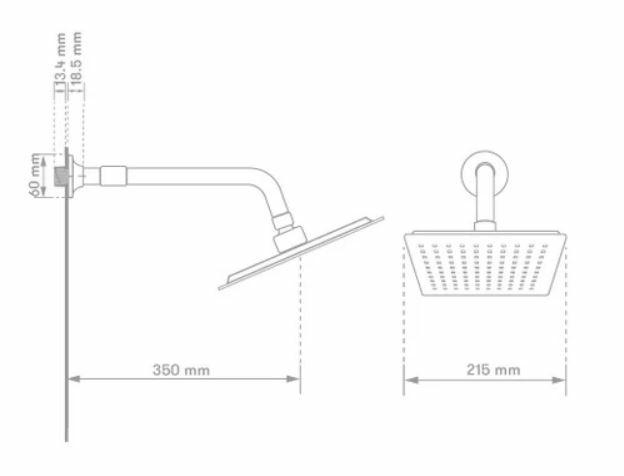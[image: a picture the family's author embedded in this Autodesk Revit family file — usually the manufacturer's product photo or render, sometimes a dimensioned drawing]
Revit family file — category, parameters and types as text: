
# Revit family: 01-1135-00 MEZCLADOR DUCHA 8 SST KRISTHAL
name_source: partatom
category: Aparatos sanitarios
units: mm (PartAtom-declared; Revit-internal decimal feet)

## family parameters
Anfitrión = Cara
Compartido = No
Corte con vacíos al cargar = No
Cota de conector redondo = Diámetro de uso
Número OmniClass = 23.31.11.00
Punto de cálculo de habitación = No
Tipo de pieza = Normal

## types (1)
- 01-1135-00
    Alto = 60 mm  [stored 0.19685 ft]
    Ancho = 60 mm  [stored 0.19685 ft]
    Conexión AC = Sí
    Conexión AF = Sí
    Conexión de residuos = No
    Conexión de ventilación = No
    Descripción = Mezclador ducha
    Distancia entre griferias = 203 mm
    Elevación por defecto = 0 mm  [stored 0 ft]
    Fabricante = Gricol
    Imagen de tipo = <Ninguno>
    Link Ficha Tecnica = https://infotecnica.gricol.com
    Modelo = 01-1135-00
    Plastico ABS Cromado = Plastico ABS Cromado
    Plastico Acrilico Transparente = Plastico Acrilico Transparente
    Product Name = MEZCLADOR DUCHA 8 SST KRISTHAL
    Profundidad = 85 mm  [stored 0.278871 ft]
    Sepacion entre registro y ducha = 400 mm  [stored 1.31234 ft]
    URL = https://www.gricol.com

note: [stored X ft] marks values corroborated as IEEE doubles in the binary element streams (Revit-internal decimal feet)

## geometry (parser evidence)
native form markers: Blend x2, Sweep x40
no freeform markers — native parametric forms only
